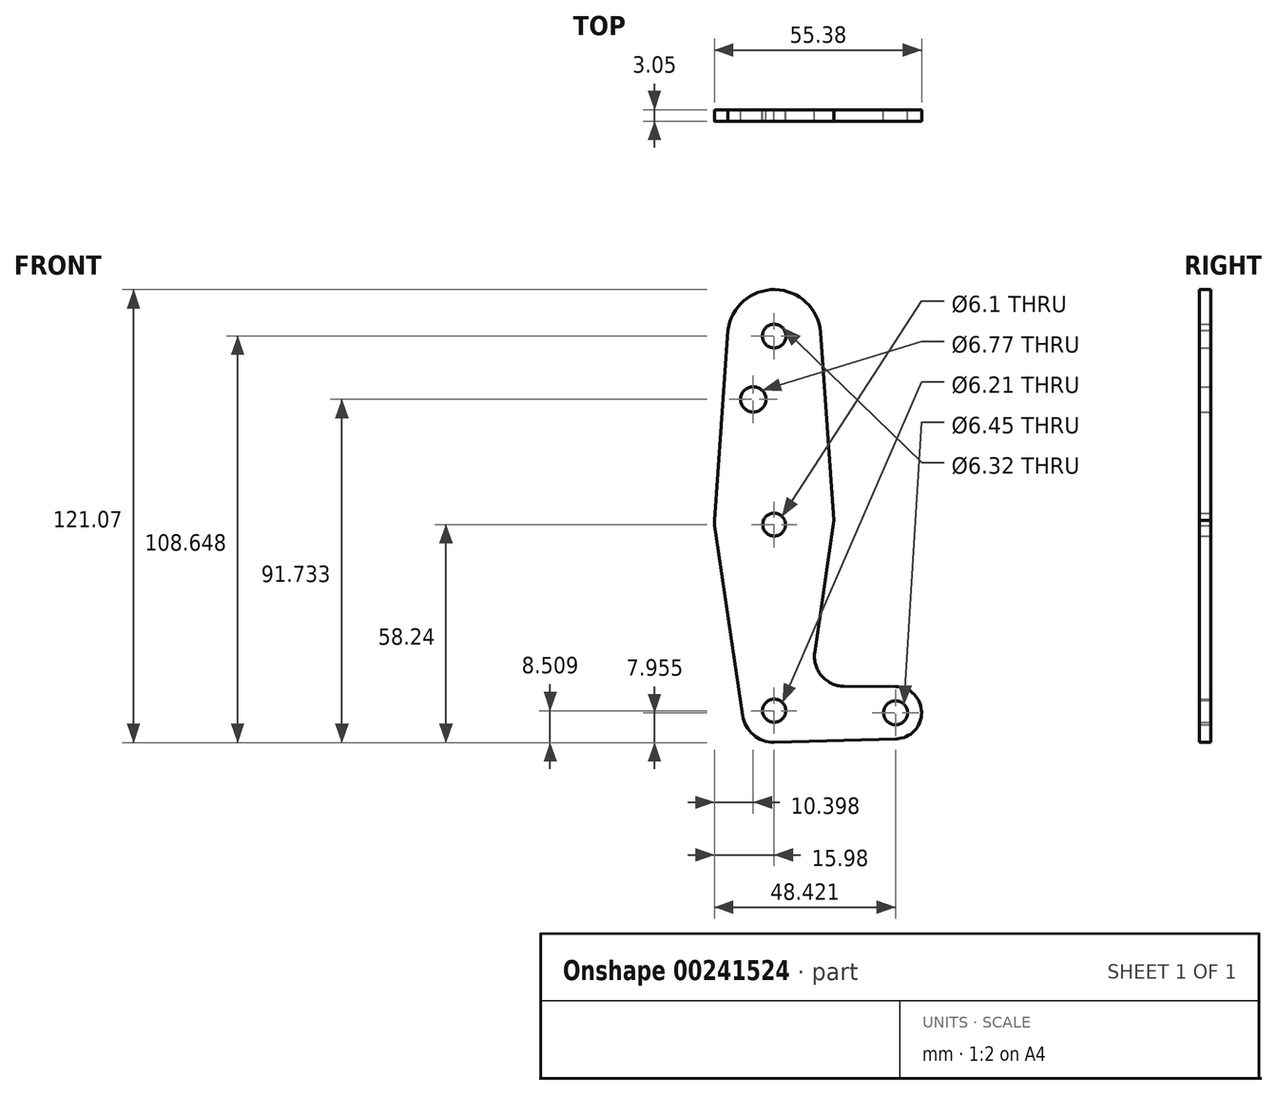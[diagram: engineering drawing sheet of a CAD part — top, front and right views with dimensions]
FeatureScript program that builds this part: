
annotation { "Feature Type Name" : "Feature", "Feature Type Description" : "" }
export const myFeature = defineFeature(function(context is Context, id is Id, definition is map)
    precondition{}
    {
        {
            var Q0;
            Q0=qCreatedBy(makeId("Front.planeOp"),FACE);
            var sketch = newSketch(context, id + "F0", { "sketchPlane" : qUnion([Q0])});
            skCircle(sketch, "E0", {"center": v(0, 0) * mm, "radius": 15.98 * mm});
            skCircle(sketch, "E1", {"center": v(0, 50.4) * mm, "radius": 12.42 * mm});
            skCircle(sketch, "E2", {"center": v(0, -49.73) * mm, "radius": 8.5 * mm});
            skCircle(sketch, "E3", {"center": v(32.44, -50.28) * mm, "radius": 6.96 * mm});
            skLineSegment(sketch, "E4", {"start": v(12.38, 51.38) * mm, "end": v(15.94, 1.13) * mm});
            skLineSegment(sketch, "E5", {"start": v(15.94, 1.13) * mm, "end": v(10.85, -34.12) * mm});
            skLineSegment(sketch, "E6", {"start": v(-12.34, 51.88) * mm, "end": v(-16.02, 0) * mm});
            skLineSegment(sketch, "E7", {"start": v(-16.02, 0) * mm, "end": v(-8.41, -50.99) * mm});
            skLineSegment(sketch, "E8", {"start": v(18.65, -43.2) * mm, "end": v(32.5, -43.32) * mm});
            skLineSegment(sketch, "E9", {"start": v(0, -58.24) * mm, "end": v(32.65, -57.24) * mm});
            skPoint(sketch, "E10.newPointB", {"position": v(0, -43.04) * mm});
            skArc(sketch, "E10.filletArc", {"start": v(10.85, -34.12) * mm, "mid": v(12.69, -40.43) * mm, "end": v(18.65, -43.2) * mm});
            skCircle(sketch, "E11", {"center": v(0, 50.4) * mm, "radius": 3.16 * mm});
            skCircle(sketch, "E12", {"center": v(-5.58, 33.5) * mm, "radius": 3.38 * mm});
            skCircle(sketch, "E13", {"center": v(0, 0) * mm, "radius": 3.05 * mm});
            skCircle(sketch, "E14", {"center": v(0, -49.73) * mm, "radius": 3.1 * mm});
            skCircle(sketch, "E15", {"center": v(32.44, -50.28) * mm, "radius": 3.23 * mm});
            skSolve(sketch);
        }
        {
            var Q0;
            {var subQ0=sQuery(id+"F0.wireOp",EDGE,"E8");Q0=makeQuery(id+"F0.imprint","IMPRINT",FACE,{"disambiguationData":[TD([[makeQuery(id+"F0.imprint","IMPRINT",EDGE,{"derivedFrom":subQ0}),-1.0]])]});}
            var Q1;
            Q1=makeQuery(id+"F0.imprint","IMPRINT",FACE,{"disambiguationData":[TD([[makeQuery(id+"F0.imprint","IMPRINT",EDGE,{"derivedFrom":sQuery(id+"F0.wireOp",EDGE,"E12")}),-1.0]])]});
            var Q2;
            Q2=makeQuery(id+"F0.imprint","IMPRINT",FACE,{"disambiguationData":[TD([[makeQuery(id+"F0.imprint","IMPRINT",EDGE,{"derivedFrom":sQuery(id+"F0.wireOp",EDGE,"E11")}),-1.0]])]});
            var Q3;
            Q3=makeQuery(id+"F0.imprint","IMPRINT",FACE,{"disambiguationData":[TD([[makeQuery(id+"F0.imprint","IMPRINT",EDGE,{"derivedFrom":sQuery(id+"F0.wireOp",EDGE,"E13")}),-1.0]])]});
            var Q4;
            Q4=makeQuery(id+"F0.imprint","IMPRINT",FACE,{"disambiguationData":[TD([[makeQuery(id+"F0.imprint","IMPRINT",EDGE,{"derivedFrom":sQuery(id+"F0.wireOp",EDGE,"E15")}),-1.0]])]});
            var Q5;
            Q5=makeQuery(id+"F0.imprint","IMPRINT",FACE,{"disambiguationData":[TD([[makeQuery(id+"F0.imprint","IMPRINT",EDGE,{"derivedFrom":sQuery(id+"F0.wireOp",EDGE,"E14")}),-1.0]])]});
            extrude(context, id + "F1", {"entities" : qUnion([Q0, Q1, Q2, Q3, Q4, Q5]), "depth" : 3.05 * mm});
        }
    });
